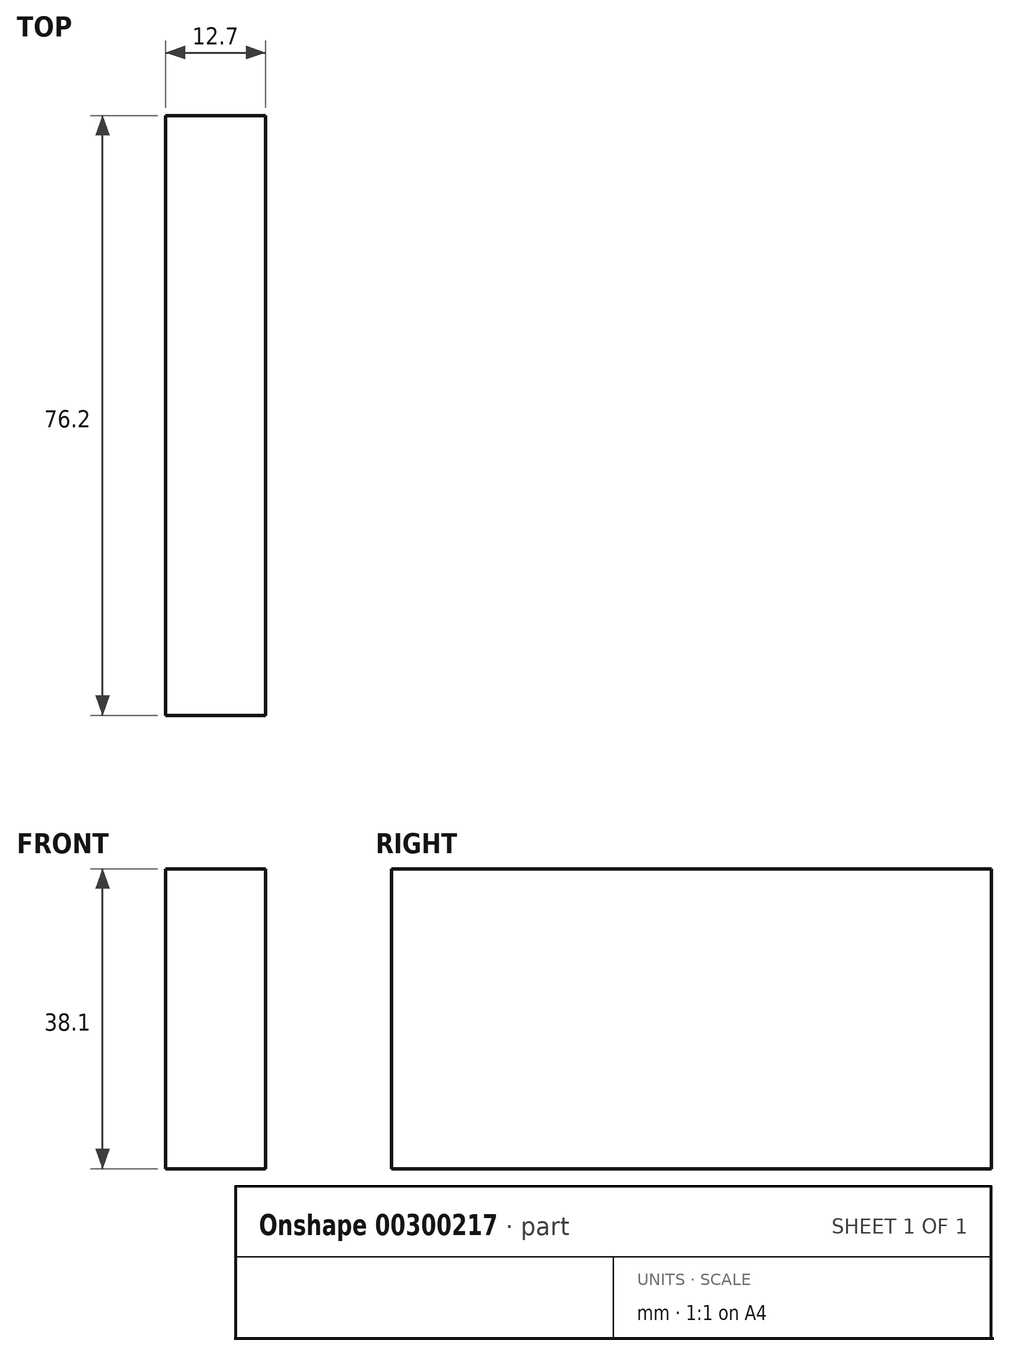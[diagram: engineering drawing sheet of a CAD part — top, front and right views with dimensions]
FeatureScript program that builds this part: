
annotation { "Feature Type Name" : "Feature", "Feature Type Description" : "" }
export const myFeature = defineFeature(function(context is Context, id is Id, definition is map)
    precondition{}
    {
        {
            var Q0;
            Q0=qCreatedBy(makeId("Right.planeOp"),FACE);
            var sketch = newSketch(context, id + "F0", { "sketchPlane" : qUnion([Q0])});
            skLineSegment(sketch, "E0.bottom", {"start": v(68.25, 22.22) * mm, "end": v(-7.95, 22.22) * mm});
            skLineSegment(sketch, "E0.top", {"start": v(68.25, -15.88) * mm, "end": v(-7.95, -15.88) * mm});
            skLineSegment(sketch, "E0.left", {"start": v(68.25, 22.22) * mm, "end": v(68.25, -15.88) * mm});
            skLineSegment(sketch, "E0.right", {"start": v(-7.95, 22.22) * mm, "end": v(-7.95, -15.88) * mm});
            skSolve(sketch);
        }
        {
            var Q0;
            Q0=makeQuery(id+"F0.imprint","IMPRINT",FACE,{"disambiguationData":[TD([[makeQuery(id+"F0.imprint","IMPRINT",EDGE,{"derivedFrom":sQuery(id+"F0.wireOp",EDGE,"E0.bottom")}),1.0]])]});
            extrude(context, id + "F1", {"entities" : qUnion([Q0]), "depth" : 12.7 * mm});
        }
    });
